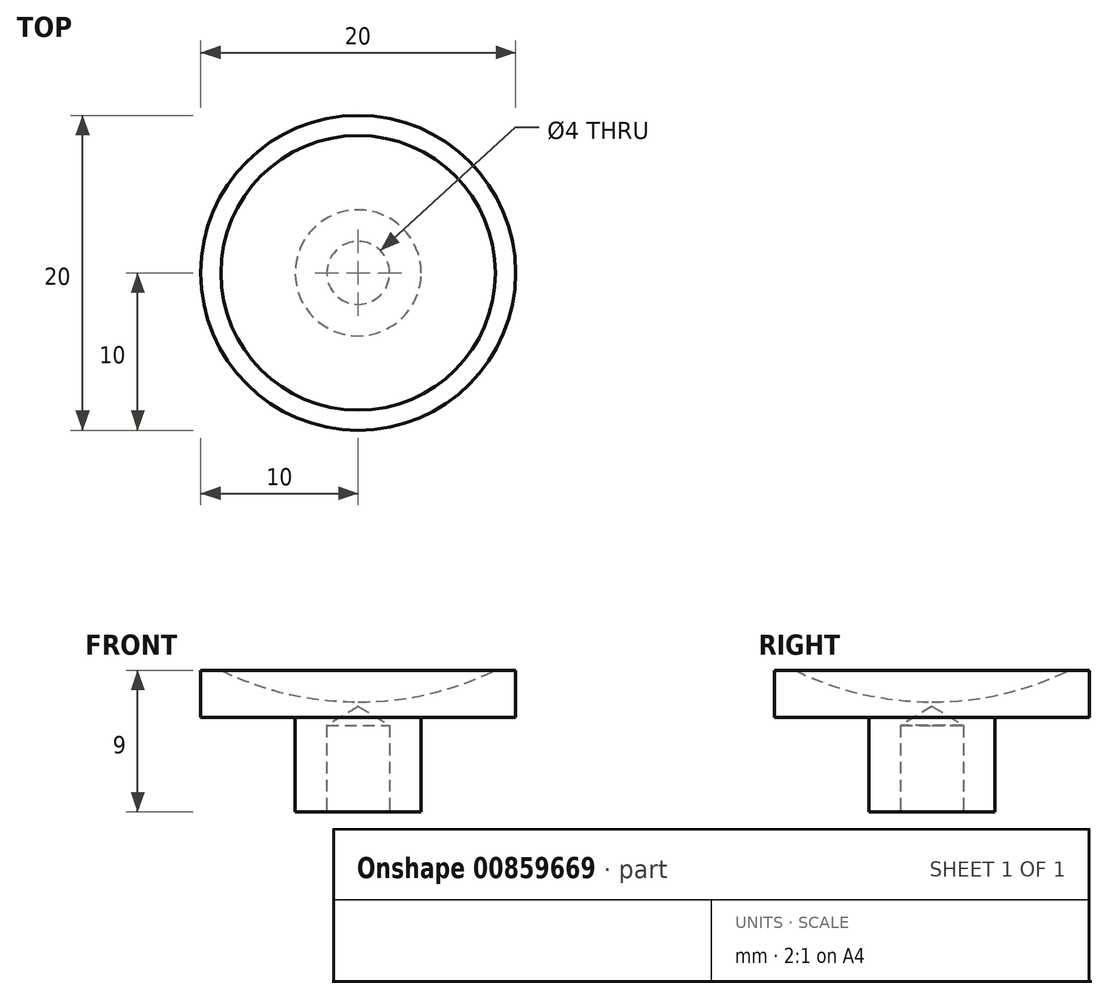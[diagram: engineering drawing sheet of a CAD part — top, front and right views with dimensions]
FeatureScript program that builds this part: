
annotation { "Feature Type Name" : "Feature", "Feature Type Description" : "" }
export const myFeature = defineFeature(function(context is Context, id is Id, definition is map)
    precondition{}
    {
        {
            var Q0;
            Q0=qCreatedBy(makeId("Top.planeOp"),FACE);
            var sketch = newSketch(context, id + "F0", { "sketchPlane" : qUnion([Q0])});
            skCircle(sketch, "E0", {"center": v(0, 0) * mm, "radius": 10 * mm});
            skSolve(sketch);
        }
        {
            var Q0;
            Q0 = qSketchRegion(id + "F0", true);
            extrude(context, id + "F1", {"entities" : qUnion([Q0]), "depth" : 3 * mm, "offsetDistance" : 25 * mm});
        }
        {
            var Q0;
            Q0=qCreatedBy(makeId("Front.planeOp"),FACE);
            var sketch = newSketch(context, id + "F2", { "sketchPlane" : qUnion([Q0])});
            skArc(sketch, "E1", {"start": v(0, 41) * mm, "mid": v(-20, 21) * mm, "end": v(0, 1) * mm});
            skLineSegment(sketch, "E2", {"start": v(0, 41) * mm, "end": v(0, 1) * mm});
            skLineSegment(sketch, "E3", {"start": v(0, 68.07) * mm, "end": v(0, -13.2) * mm, "construction": true});
            skLineSegment(sketch, "E4", {"start": v(-10.03, 3.03) * mm, "end": v(0, 3.03) * mm, "construction": true});
            skLineSegment(sketch, "E5", {"start": v(-8.78, 3.03) * mm, "end": v(-8.78, 3.65) * mm, "construction": true});
            skSolve(sketch);
        }
        {
            var Q0;
            Q0 = qSketchRegion(id + "F2", true);
            var Q1;
            Q1=sQuery(id+"F2.wireOp",EDGE,"E3");
            revolve(context, id + "F3", {"operationType" : NewBodyOperationType.REMOVE, "surfaceOperationType" : NewSurfaceOperationType.NEW, "entities" : qUnion([Q0]), "axis" : qUnion([Q1]), "revolveType" : RevolveType.FULL, "oppositeDirection" : true});
        }
        {
            var Q0;
            Q0=makeQuery(id+"F1.opExtrude","CAP_FACE",FACE,{"disambiguationData":[OSD([sQuery(id+"F0.wireOp",EDGE,"E0")])],"isStart":true});
            var sketch = newSketch(context, id + "F4", { "sketchPlane" : qUnion([Q0])});
            skCircle(sketch, "E6", {"center": v(0, 0) * mm, "radius": 4 * mm});
            skSolve(sketch);
        }
        {
            var Q0;
            Q0 = qSketchRegion(id + "F4", true);
            extrude(context, id + "F5", {"entities" : qUnion([Q0]), "operationType" : NewBodyOperationType.ADD, "depth" : 6 * mm, "offsetDistance" : 25 * mm});
        }
        {
            var Q0;
            Q0=makeQuery(id+"F5.opExtrude","CAP_FACE",FACE,{"disambiguationData":[OSD([sQuery(id+"F4.wireOp",EDGE,"E6")])],"isStart":false});
            var sketch = newSketch(context, id + "F6", { "sketchPlane" : qUnion([Q0])});
            skPoint(sketch, "E7", {"position": v(0, 0) * mm});
            skSolve(sketch);
        }
        {
            var Q0;
            Q0=sQuery(id+"F6.wireOp",VERTEX,"E7");
            var Q1;
            Q1=makeQuery(id+"F1.opExtrude","SWEPT_BODY",BODY,{"disambiguationData":[OSD([sQuery(id+"F0.wireOp",EDGE,"E0")])]});
            hole(context, id + "F7", {"style" : HoleStyle.SIMPLE, "endStyle" : HoleEndStyle.BLIND, "holeDiameter" : 4 * mm, "majorDiameter" : 5 * mm, "holeDepth" : 5.5 * mm, "isTappedThrough" : true, "tappedDepth" : 12 * mm, "tapClearance" : 3, "locations" : qUnion([Q0]), "scope" : qUnion([Q1])});
        }
    });
